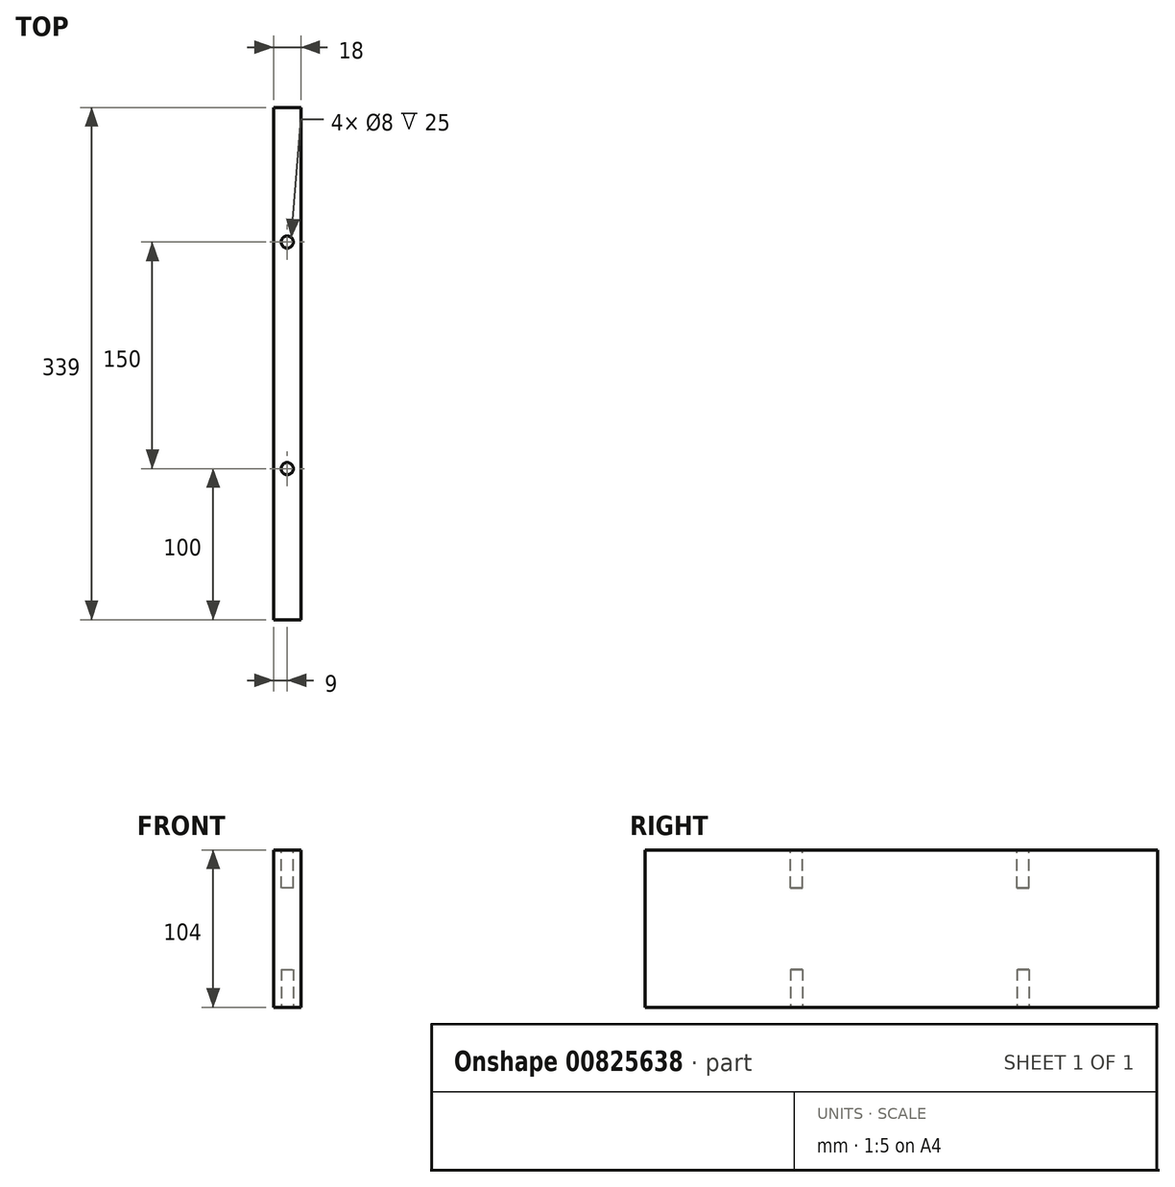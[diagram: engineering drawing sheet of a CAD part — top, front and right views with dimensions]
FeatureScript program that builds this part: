
annotation { "Feature Type Name" : "Feature", "Feature Type Description" : "" }
export const myFeature = defineFeature(function(context is Context, id is Id, definition is map)
    precondition{}
    {
        {
            var Q0;
            Q0=qCreatedBy(makeId("Front.planeOp"),FACE);
            var sketch = newSketch(context, id + "F0", { "sketchPlane" : qUnion([Q0])});
            skLineSegment(sketch, "E0.bottom", {"start": v(0, 104) * mm, "end": v(18, 104) * mm});
            skLineSegment(sketch, "E0.top", {"start": v(0, 0) * mm, "end": v(18, 0) * mm});
            skLineSegment(sketch, "E0.left", {"start": v(0, 104) * mm, "end": v(0, 0) * mm});
            skLineSegment(sketch, "E0.right", {"start": v(18, 104) * mm, "end": v(18, 0) * mm});
            skSolve(sketch);
        }
        {
            var Q0;
            Q0=makeQuery(id+"F0.imprint","IMPRINT",FACE,{"disambiguationData":[TD([[makeQuery(id+"F0.imprint","IMPRINT",EDGE,{"derivedFrom":sQuery(id+"F0.wireOp",EDGE,"E0.bottom")}),-1.0]])]});
            extrude(context, id + "F1", {"entities" : qUnion([Q0]), "depth" : 339 * mm, "offsetDistance" : 25 * mm});
        }
        {
            var Q0;
            Q0=makeQuery(id+"F1.opExtrude","SWEPT_FACE",FACE,{"disambiguationData":[OSD([sQuery(id+"F0.wireOp",EDGE,"E0.bottom")])]});
            var sketch = newSketch(context, id + "F2", { "sketchPlane" : qUnion([Q0])});
            skCircle(sketch, "E1", {"center": v(9, -89) * mm, "radius": 4 * mm});
            skCircle(sketch, "E2", {"center": v(9, -239) * mm, "radius": 4 * mm});
            skSolve(sketch);
        }
        {
            var Q0;
            Q0=makeQuery(id+"F2.imprint","IMPRINT",FACE,{"disambiguationData":[TD([[makeQuery(id+"F2.imprint","IMPRINT",EDGE,{"derivedFrom":sQuery(id+"F2.wireOp",EDGE,"E1")}),1.0]])]});
            var Q1;
            Q1=makeQuery(id+"F2.imprint","IMPRINT",FACE,{"disambiguationData":[TD([[makeQuery(id+"F2.imprint","IMPRINT",EDGE,{"derivedFrom":sQuery(id+"F2.wireOp",EDGE,"E2")}),1.0]])]});
            extrude(context, id + "F3", {"entities" : qUnion([Q0, Q1]), "operationType" : NewBodyOperationType.REMOVE, "oppositeDirection" : true, "depth" : 25 * mm, "offsetDistance" : 25 * mm});
        }
        {
            var Q0;
            Q0=makeQuery(id+"F1.opExtrude","SWEPT_FACE",FACE,{"disambiguationData":[OSD([sQuery(id+"F0.wireOp",EDGE,"E0.top")])]});
            var sketch = newSketch(context, id + "F4", { "sketchPlane" : qUnion([Q0])});
            skCircle(sketch, "E3", {"center": v(9, 89) * mm, "radius": 4 * mm});
            skCircle(sketch, "E4", {"center": v(9, 239) * mm, "radius": 4 * mm});
            skSolve(sketch);
        }
        {
            var Q0;
            Q0=makeQuery(id+"F4.imprint","IMPRINT",FACE,{"disambiguationData":[TD([[makeQuery(id+"F4.imprint","IMPRINT",EDGE,{"derivedFrom":sQuery(id+"F4.wireOp",EDGE,"E3")}),1.0]])]});
            var Q1;
            Q1=makeQuery(id+"F4.imprint","IMPRINT",FACE,{"disambiguationData":[TD([[makeQuery(id+"F4.imprint","IMPRINT",EDGE,{"derivedFrom":sQuery(id+"F4.wireOp",EDGE,"E4")}),1.0]])]});
            extrude(context, id + "F5", {"entities" : qUnion([Q0, Q1]), "operationType" : NewBodyOperationType.REMOVE, "oppositeDirection" : true, "depth" : 25 * mm, "offsetDistance" : 25 * mm});
        }
    });
